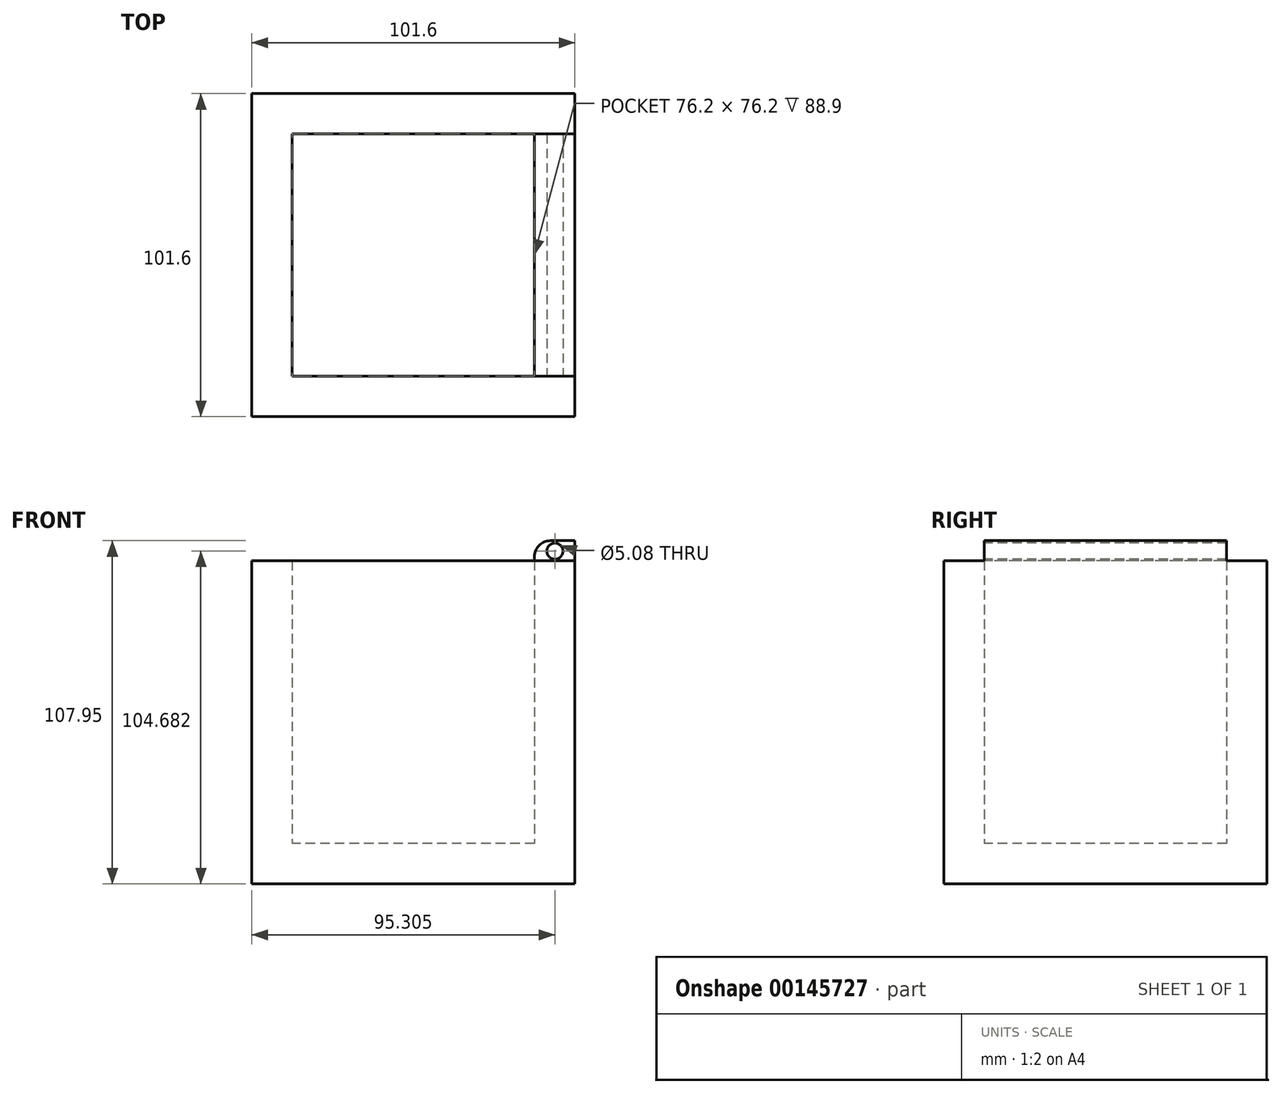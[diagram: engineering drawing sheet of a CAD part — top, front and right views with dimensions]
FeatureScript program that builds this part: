
annotation { "Feature Type Name" : "Feature", "Feature Type Description" : "" }
export const myFeature = defineFeature(function(context is Context, id is Id, definition is map)
    precondition{}
    {
        {
            var Q0;
            Q0=qCreatedBy(makeId("Top.planeOp"),FACE);
            var sketch = newSketch(context, id + "F0", { "sketchPlane" : qUnion([Q0])});
            skLineSegment(sketch, "E0.bottom", {"start": v(50.8, 50.8) * mm, "end": v(-50.8, 50.8) * mm});
            skLineSegment(sketch, "E0.top", {"start": v(50.8, -50.8) * mm, "end": v(-50.8, -50.8) * mm});
            skLineSegment(sketch, "E0.left", {"start": v(50.8, 50.8) * mm, "end": v(50.8, -50.8) * mm});
            skLineSegment(sketch, "E0.right", {"start": v(-50.8, 50.8) * mm, "end": v(-50.8, -50.8) * mm});
            skSolve(sketch);
        }
        {
            var Q0;
            Q0=makeQuery(id+"F0.imprint","IMPRINT",FACE,{"disambiguationData":[TD([[makeQuery(id+"F0.imprint","IMPRINT",EDGE,{"derivedFrom":sQuery(id+"F0.wireOp",EDGE,"E0.bottom")}),1.0]])]});
            extrude(context, id + "F1", {"entities" : qUnion([Q0]), "depth" : 101.6 * mm});
        }
        {
            var Q0;
            Q0=makeQuery(id+"F1.opExtrude","CAP_FACE",FACE,{"disambiguationData":[OSD([sQuery(id+"F0.wireOp",EDGE,"E0.bottom"),sQuery(id+"F0.wireOp",EDGE,"E0.top"),sQuery(id+"F0.wireOp",EDGE,"E0.left"),sQuery(id+"F0.wireOp",EDGE,"E0.right")])],"isStart":false});
            shell(context, id + "F2", {"entities" : qUnion([Q0]), "thickness" : 12.7 * mm});
        }
        {
            var Q0;
            Q0=makeQuery(id+"F1.opExtrude","CAP_FACE",FACE,{"disambiguationData":[OSD([sQuery(id+"F0.wireOp",EDGE,"E0.bottom"),sQuery(id+"F0.wireOp",EDGE,"E0.top"),sQuery(id+"F0.wireOp",EDGE,"E0.left"),sQuery(id+"F0.wireOp",EDGE,"E0.right")])],"isStart":false});
            var sketch = newSketch(context, id + "F3", { "sketchPlane" : qUnion([Q0])});
            skLineSegment(sketch, "E1.bottom", {"start": v(38.1, -38.1) * mm, "end": v(50.8, -38.1) * mm});
            skLineSegment(sketch, "E1.top", {"start": v(38.1, 38.1) * mm, "end": v(50.8, 38.1) * mm});
            skLineSegment(sketch, "E1.left", {"start": v(38.1, -38.1) * mm, "end": v(38.1, 38.1) * mm});
            skLineSegment(sketch, "E1.right", {"start": v(50.8, -38.1) * mm, "end": v(50.8, 38.1) * mm});
            skSolve(sketch);
        }
        {
            var Q0;
            Q0 = qSketchRegion(id + "F3", true);
            extrude(context, id + "F4", {"entities" : qUnion([Q0]), "operationType" : NewBodyOperationType.ADD, "depth" : 6.35 * mm});
        }
        {
            var Q0;
            Q0=makeQuery(id+"F4.opExtrude","SWEPT_FACE",FACE,{"disambiguationData":[OSD([sQuery(id+"F3.wireOp",EDGE,"E1.bottom")])]});
            var sketch = newSketch(context, id + "F5", { "sketchPlane" : qUnion([Q0])});
            skCircle(sketch, "E2", {"center": v(44.5, 104.68) * mm, "radius": 2.54 * mm});
            skLineSegment(sketch, "E3", {"start": v(38.1, 104.78) * mm, "end": v(44.5, 104.68) * mm, "construction": true});
            skLineSegment(sketch, "E4", {"start": v(50.8, 104.68) * mm, "end": v(44.5, 104.68) * mm, "construction": true});
            skSolve(sketch);
        }
        {
            var Q0;
            Q0 = qSketchRegion(id + "F5", true);
            extrude(context, id + "F6", {"entities" : qUnion([Q0]), "operationType" : NewBodyOperationType.REMOVE, "oppositeDirection" : true, "depth" : 95.88 * mm});
        }
        {
            var Q0;
            Q0=makeQuery(id+"F4.opExtrude","CAP_EDGE",EDGE,{"disambiguationData":[OSD([sQuery(id+"F3.wireOp",EDGE,"E1.left")])],"isStart":false});
            fillet(context, id + "F7", {"entities" : qUnion([Q0]), "radius" : 5.08 * mm, "tangentPropagation" : true, "allowEdgeOverflow" : false});
        }
    });
